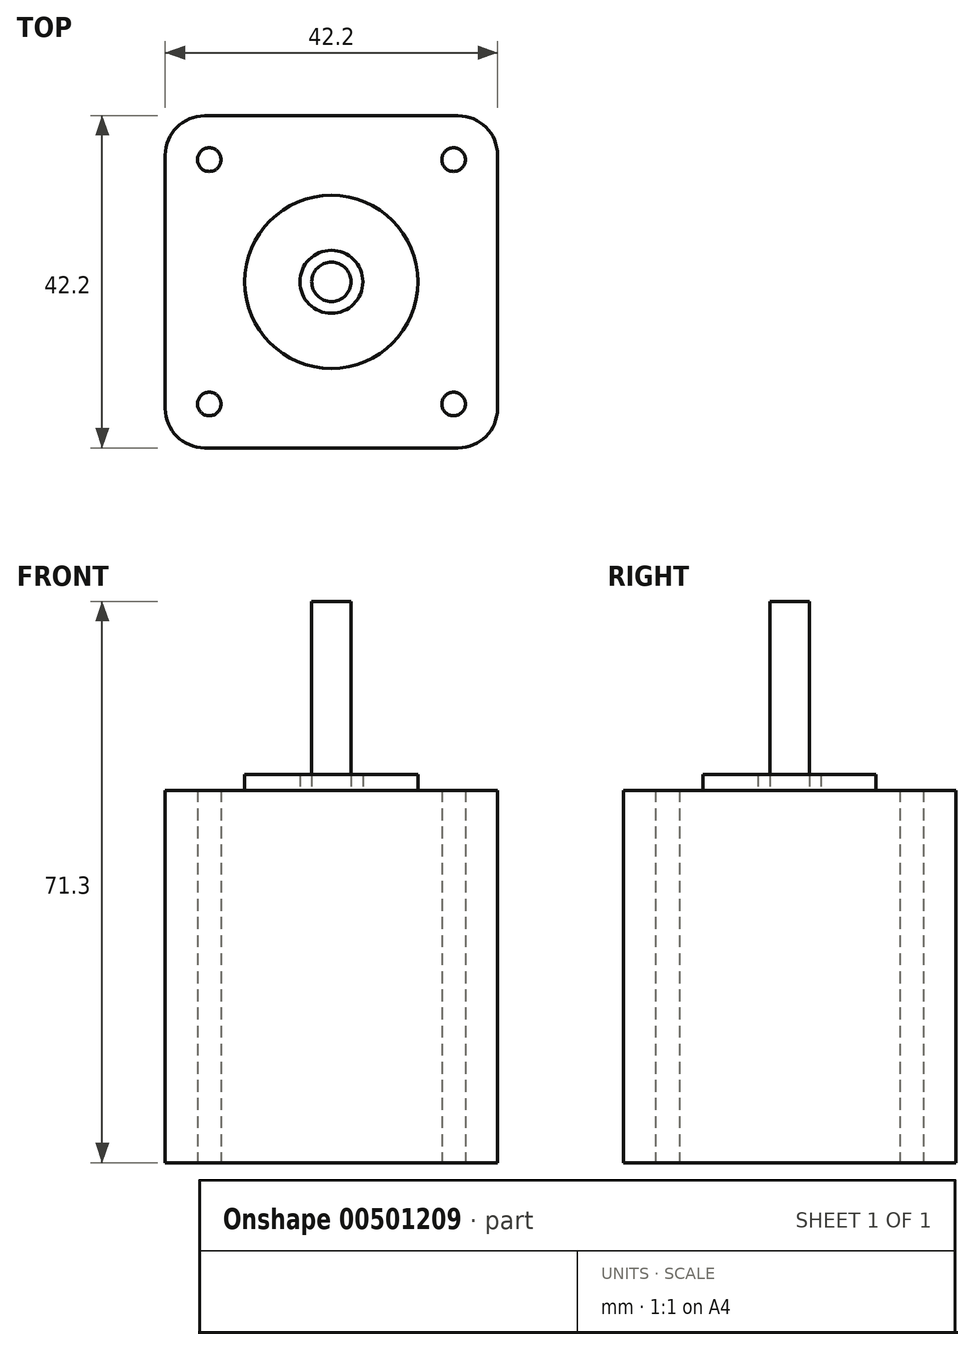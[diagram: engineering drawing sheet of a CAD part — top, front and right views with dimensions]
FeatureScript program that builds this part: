
annotation { "Feature Type Name" : "Feature", "Feature Type Description" : "" }
export const myFeature = defineFeature(function(context is Context, id is Id, definition is map)
    precondition{}
    {
        {
            var Q0;
            Q0=qCreatedBy(makeId("Top.planeOp"),FACE);
            var sketch = newSketch(context, id + "F0", { "sketchPlane" : qUnion([Q0])});
            skLineSegment(sketch, "E0.rect.bottom", {"start": v(-16.1, 21.1) * mm, "end": v(16.1, 21.1) * mm});
            skLineSegment(sketch, "E0.rect.top", {"start": v(-16.1, -21.1) * mm, "end": v(16.1, -21.1) * mm});
            skLineSegment(sketch, "E0.rect.left", {"start": v(-21.1, 16.1) * mm, "end": v(-21.1, -16.1) * mm});
            skLineSegment(sketch, "E0.rect.right", {"start": v(21.1, 16.1) * mm, "end": v(21.1, -16.1) * mm});
            skPoint(sketch, "E0.rect.middle", {"position": v(0, 0) * mm});
            skCircle(sketch, "E1", {"center": v(-15.52, 15.52) * mm, "radius": 1.5 * mm});
            skPoint(sketch, "E2.visualSharp", {"position": v(-21.1, 21.1) * mm});
            skArc(sketch, "E2.filletArc", {"start": v(-16.1, 21.1) * mm, "mid": v(-19.64, 19.64) * mm, "end": v(-21.1, 16.1) * mm});
            skPoint(sketch, "E3.visualSharp", {"position": v(21.1, 21.1) * mm});
            skArc(sketch, "E3.filletArc", {"start": v(21.1, 16.1) * mm, "mid": v(19.64, 19.64) * mm, "end": v(16.1, 21.1) * mm});
            skPoint(sketch, "E4.visualSharp", {"position": v(21.1, -21.1) * mm});
            skArc(sketch, "E4.filletArc", {"start": v(16.1, -21.1) * mm, "mid": v(19.64, -19.64) * mm, "end": v(21.1, -16.1) * mm});
            skPoint(sketch, "E5.visualSharp", {"position": v(-21.1, -21.1) * mm});
            skArc(sketch, "E5.filletArc", {"start": v(-21.1, -16.1) * mm, "mid": v(-19.64, -19.64) * mm, "end": v(-16.1, -21.1) * mm});
            skCircle(sketch, "E6", {"center": v(15.52, 15.52) * mm, "radius": 1.5 * mm});
            skCircle(sketch, "E7", {"center": v(-15.52, -15.52) * mm, "radius": 1.5 * mm});
            skCircle(sketch, "E8", {"center": v(15.52, -15.52) * mm, "radius": 1.5 * mm});
            skSolve(sketch);
        }
        {
            var Q0;
            Q0=makeQuery(id+"F0.imprint","IMPRINT",FACE,{"disambiguationData":[TD([[makeQuery(id+"F0.imprint","IMPRINT",EDGE,{"derivedFrom":sQuery(id+"F0.wireOp",EDGE,"E0.rect.bottom")}),-1.0]])]});
            extrude(context, id + "F1", {"entities" : qUnion([Q0]), "depth" : 47.3 * mm});
        }
        {
            var Q0;
            Q0=makeQuery(id+"F1.opExtrude","CAP_FACE",FACE,{"disambiguationData":[OSD([sQuery(id+"F0.wireOp",EDGE,"E0.rect.bottom"),sQuery(id+"F0.wireOp",EDGE,"E0.rect.top"),sQuery(id+"F0.wireOp",EDGE,"E0.rect.left"),sQuery(id+"F0.wireOp",EDGE,"E0.rect.right"),sQuery(id+"F0.wireOp",EDGE,"E1"),sQuery(id+"F0.wireOp",EDGE,"E2.filletArc"),sQuery(id+"F0.wireOp",EDGE,"E3.filletArc"),sQuery(id+"F0.wireOp",EDGE,"E4.filletArc"),sQuery(id+"F0.wireOp",EDGE,"E5.filletArc"),sQuery(id+"F0.wireOp",EDGE,"E6"),sQuery(id+"F0.wireOp",EDGE,"E7"),sQuery(id+"F0.wireOp",EDGE,"E8")])],"isStart":false});
            var sketch = newSketch(context, id + "F2", { "sketchPlane" : qUnion([Q0])});
            skCircle(sketch, "E9", {"center": v(0, 0) * mm, "radius": 11 * mm});
            skCircle(sketch, "E10", {"center": v(0, 0) * mm, "radius": 4 * mm});
            skSolve(sketch);
        }
        {
            var Q0;
            Q0=makeQuery(id+"F2.imprint","IMPRINT",FACE,{"disambiguationData":[TD([[makeQuery(id+"F2.imprint","IMPRINT",EDGE,{"derivedFrom":sQuery(id+"F2.wireOp",EDGE,"E9")}),1.0]])]});
            extrude(context, id + "F3", {"entities" : qUnion([Q0]), "operationType" : NewBodyOperationType.ADD, "depth" : 2 * mm});
        }
        {
            var Q0;
            {var subQ0=sQuery(id+"F0.wireOp",EDGE,"E6");var subQ1=sQuery(id+"F0.wireOp",EDGE,"E4.filletArc");var subQ2=sQuery(id+"F0.wireOp",EDGE,"E3.filletArc");var subQ3=sQuery(id+"F0.wireOp",EDGE,"E2.filletArc");var subQ4=sQuery(id+"F0.wireOp",EDGE,"E1");var subQ5=sQuery(id+"F0.wireOp",EDGE,"E0.rect.bottom");var subQ6=sQuery(id+"F0.wireOp",EDGE,"E5.filletArc");var subQ7=sQuery(id+"F0.wireOp",EDGE,"E0.rect.top");var subQ8=sQuery(id+"F0.wireOp",EDGE,"E0.rect.left");var subQ9=sQuery(id+"F0.wireOp",EDGE,"E0.rect.right");var subQ10=sQuery(id+"F0.wireOp",EDGE,"E7");var subQ11=sQuery(id+"F0.wireOp",EDGE,"E8");Q0=makeQuery(id+"F3.boolean.opBoolean","SPLIT",FACE,{"disambiguationData":[TD([makeQuery(id+"F1.opExtrude","SWEPT_FACE",FACE,{"disambiguationData":[OSD([subQ5])]})])],"derivedFrom":makeQuery(id+"F1.opExtrude","CAP_FACE",FACE,{"disambiguationData":[OSD([subQ5,subQ7,subQ8,subQ9,subQ4,subQ3,subQ2,subQ1,subQ6,subQ0,subQ10,subQ11])],"isStart":false})});}
            var sketch = newSketch(context, id + "F4", { "sketchPlane" : qUnion([Q0])});
            skCircle(sketch, "E11", {"center": v(0, 0) * mm, "radius": 2.5 * mm});
            skSolve(sketch);
        }
        {
            var Q0;
            Q0=makeQuery(id+"F4.imprint","IMPRINT",FACE,{"disambiguationData":[TD([[makeQuery(id+"F4.imprint","IMPRINT",EDGE,{"derivedFrom":sQuery(id+"F4.wireOp",EDGE,"E11")}),1.0]])]});
            extrude(context, id + "F5", {"entities" : qUnion([Q0]), "operationType" : NewBodyOperationType.ADD, "depth" : 24 * mm});
        }
    });
